# Revit family: No interlocked sockets 440_460 V
name_source: partatom
category: Installations électriques
revit_build: Autodesk Revit 2018 (Build: 20170223_1515(x64)
units: mm (PartAtom-declared; Revit-internal decimal feet)

## family parameters
Conserver l'orientation des annotations = Non
Cote de connecteur circulaire = Utiliser le diamètre
Couper avec des vides une fois chargée = Non
Hôte = Face
Partagée = Non
Point de calcul de pièce = Non
Type d'élément = Normal

## types (2) — shared parameters
Elévation par défaut = 1000 mm  [stored 3.28084 ft]
Fabricant = Legrand
Flush E or Surface mounting S = flush and surface mounting
International standard socket for flush mounting or surface mounting with accessory allows the connection of power devices = International standard socket for flush mounting or surface mounting with accessory allows the connection of power devices
Maximum use temperature = 40
Minimum installation temperature = -5
Minimum use temperature = -25
Number of poles = 4
Product family = 0854-P17 TEMPRA PRO
Standard IEC or NFC = IEC
Tension V = 400 440 V  50 60 Hz red
characteristic color = red
connecting type = screw terminals
height mm = 84 mm  [stored 0.275591 ft]
horizontal fixing distance mm = 70 mm
material of box = plastic
resistance to chocks IK = 9
vertical fixing distance mm = 70 mm
width mm = 84 mm  [stored 0.275591 ft]

## per-type parameters (varying)
| type | Description | Position of earth h | depth for flush mounting mm | depth mm | halogen free | intensity A | protection class IP |
| P17 Refrigerated container | LG-555491_Panel mounting socket P17 for refrigerated containers | 3 | 42 mm | 92 mm  [stored 0.301837 ft] | Non | 32 A |  |
| P17 - 16A - 3P+E - IP44 | LG-555190_Panel mounting socket P17  16A 3P+E 440/460V IP44 | 11 | 36 mm | 74 mm | Oui | 16 A | IP44 |

note: [stored X ft] marks values corroborated as IEEE doubles in the binary element streams (Revit-internal decimal feet)
